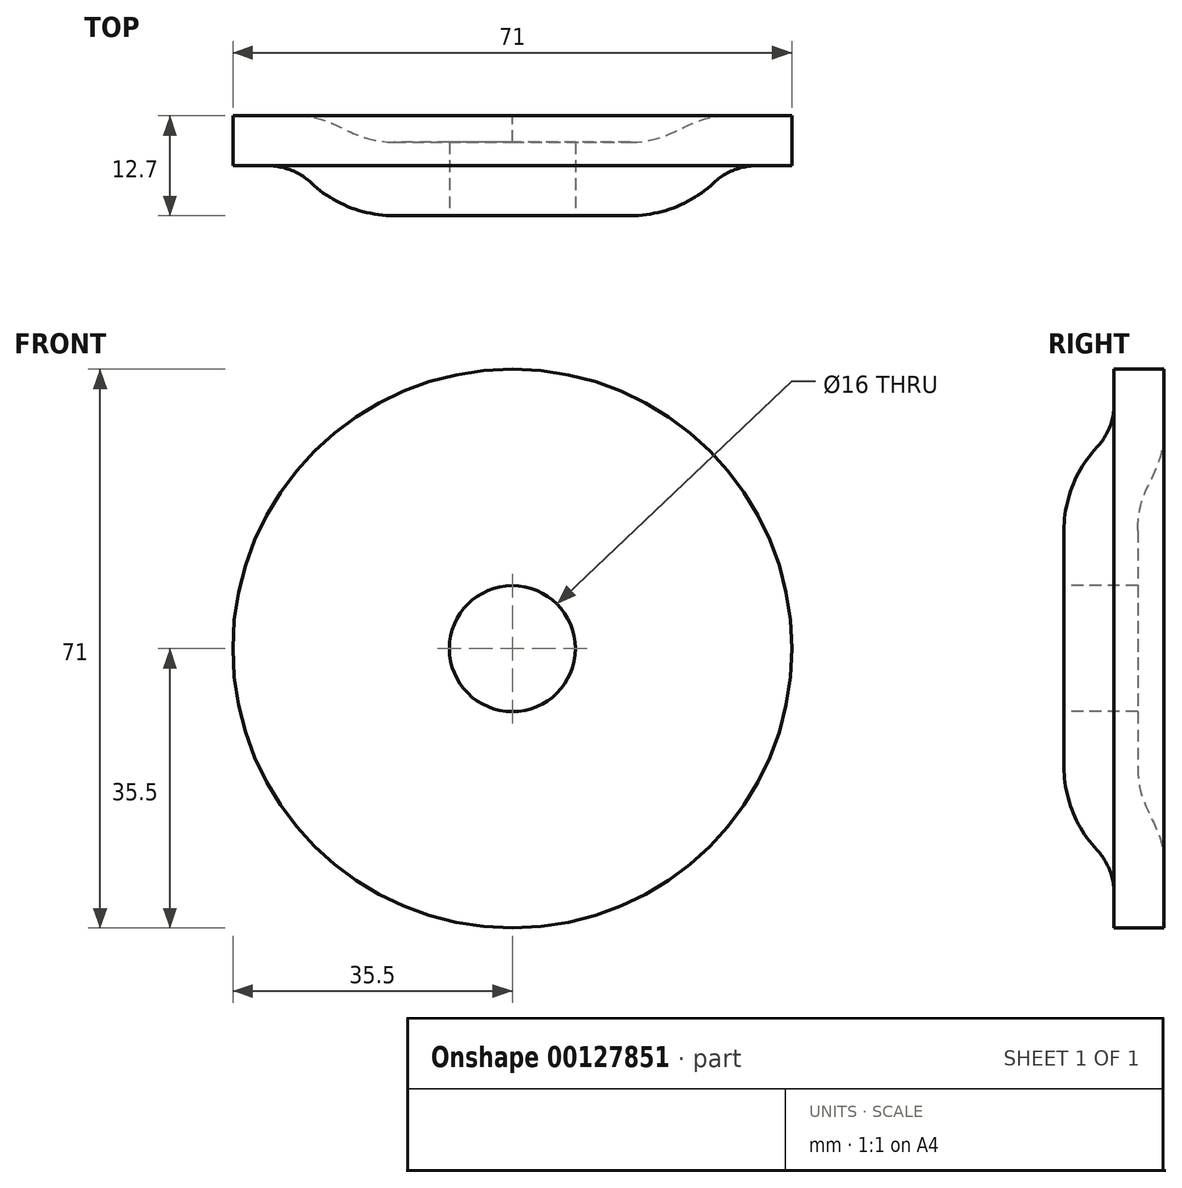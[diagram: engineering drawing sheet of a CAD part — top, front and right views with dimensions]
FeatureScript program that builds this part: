
annotation { "Feature Type Name" : "Feature", "Feature Type Description" : "" }
export const myFeature = defineFeature(function(context is Context, id is Id, definition is map)
    precondition{}
    {
        {
            var Q0;
            Q0=qCreatedBy(makeId("Right.planeOp"),FACE);
            var sketch = newSketch(context, id + "F0", { "sketchPlane" : qUnion([Q0])});
            skPoint(sketch, "E0", {"position": v(0, 35.5) * mm});
            skPoint(sketch, "E1", {"position": v(0, 0) * mm});
            skPoint(sketch, "E2", {"position": v(-12.7, 0) * mm});
            skPoint(sketch, "E3", {"position": v(-12.7, 15) * mm});
            skPoint(sketch, "E4", {"position": v(-6.35, 35.5) * mm});
            skPoint(sketch, "E5", {"position": v(-6.35, 27.5) * mm});
            skLineSegment(sketch, "E6", {"start": v(-12.7, 0) * mm, "end": v(-3.35, 0) * mm});
            skLineSegment(sketch, "E7", {"start": v(0, 27.5) * mm, "end": v(0, 35.5) * mm});
            skLineSegment(sketch, "E8", {"start": v(0, 35.5) * mm, "end": v(-6.35, 35.5) * mm});
            skLineSegment(sketch, "E9", {"start": v(-6.35, 35.5) * mm, "end": v(-6.35, 27.5) * mm});
            skLineSegment(sketch, "E10", {"start": v(-12.7, 15) * mm, "end": v(-12.7, 0) * mm});
            skArc(sketch, "E11", {"start": v(-6.35, 27.5) * mm, "mid": v(-11.02, 22.01) * mm, "end": v(-12.7, 15) * mm});
            skPoint(sketch, "E12", {"position": v(0, 27.5) * mm});
            skPoint(sketch, "E13", {"position": v(-3.35, 15) * mm});
            skPoint(sketch, "E14", {"position": v(0, 15) * mm});
            skPoint(sketch, "E15", {"position": v(-3.35, 0) * mm});
            skLineSegment(sketch, "E16", {"start": v(-3.35, 0) * mm, "end": v(-3.35, 15) * mm});
            skFitSpline(sketch, "E17", {"points": [v(-3.35, 15) * mm, v(0, 27.5) * mm], "startDerivative": vector(0, 17.48) * mm, "endDerivative": vector(0, 16.42) * mm});
            skLineSegment(sketch, "E18", {"start": v(0, 0) * mm, "end": v(-19, 0) * mm, "construction": true});
            skSolve(sketch);
        }
        {
            var Q0;
            Q0=makeQuery(id+"F0.imprint","IMPRINT",FACE,{"disambiguationData":[TD([[makeQuery(id+"F0.imprint","IMPRINT",EDGE,{"derivedFrom":sQuery(id+"F0.wireOp",EDGE,"E6")}),1.0]])]});
            var Q1;
            Q1=sQuery(id+"F0.wireOp",EDGE,"E18");
            revolve(context, id + "F1", {"entities" : qUnion([Q0]), "axis" : qUnion([Q1]), "revolveType" : RevolveType.FULL});
        }
        {
            var Q0;
            Q0=makeQuery(id+"F1.opRevolve","SWEPT_FACE",FACE,{"disambiguationData":[OSD([sQuery(id+"F0.wireOp",EDGE,"E10")])]});
            var sketch = newSketch(context, id + "F2", { "sketchPlane" : qUnion([Q0])});
            skCircle(sketch, "E19", {"center": v(0, 0) * mm, "radius": 8 * mm});
            skSolve(sketch);
        }
        {
            var Q0;
            Q0=qSketchRegion(id+"F2",true);
            extrude(context, id + "F3", {"entities" : qUnion([Q0]), "operationType" : NewBodyOperationType.REMOVE, "endBound" : BoundingType.THROUGH_ALL, "oppositeDirection" : true, "depth" : 25 * mm});
        }
        {
            var Q0;
            Q0=makeQuery(id+"F1.opRevolve","SWEPT_EDGE",EDGE,{"disambiguationData":[OSD([sQuery(id+"F0.wireOp",EDGE,"E9"),sQuery(id+"F0.wireOp",EDGE,"E11")])]});
            fillet(context, id + "F4", {"entities" : qUnion([Q0]), "radius" : 8 * mm, "tangentPropagation" : true, "allowEdgeOverflow" : false});
        }
    });
